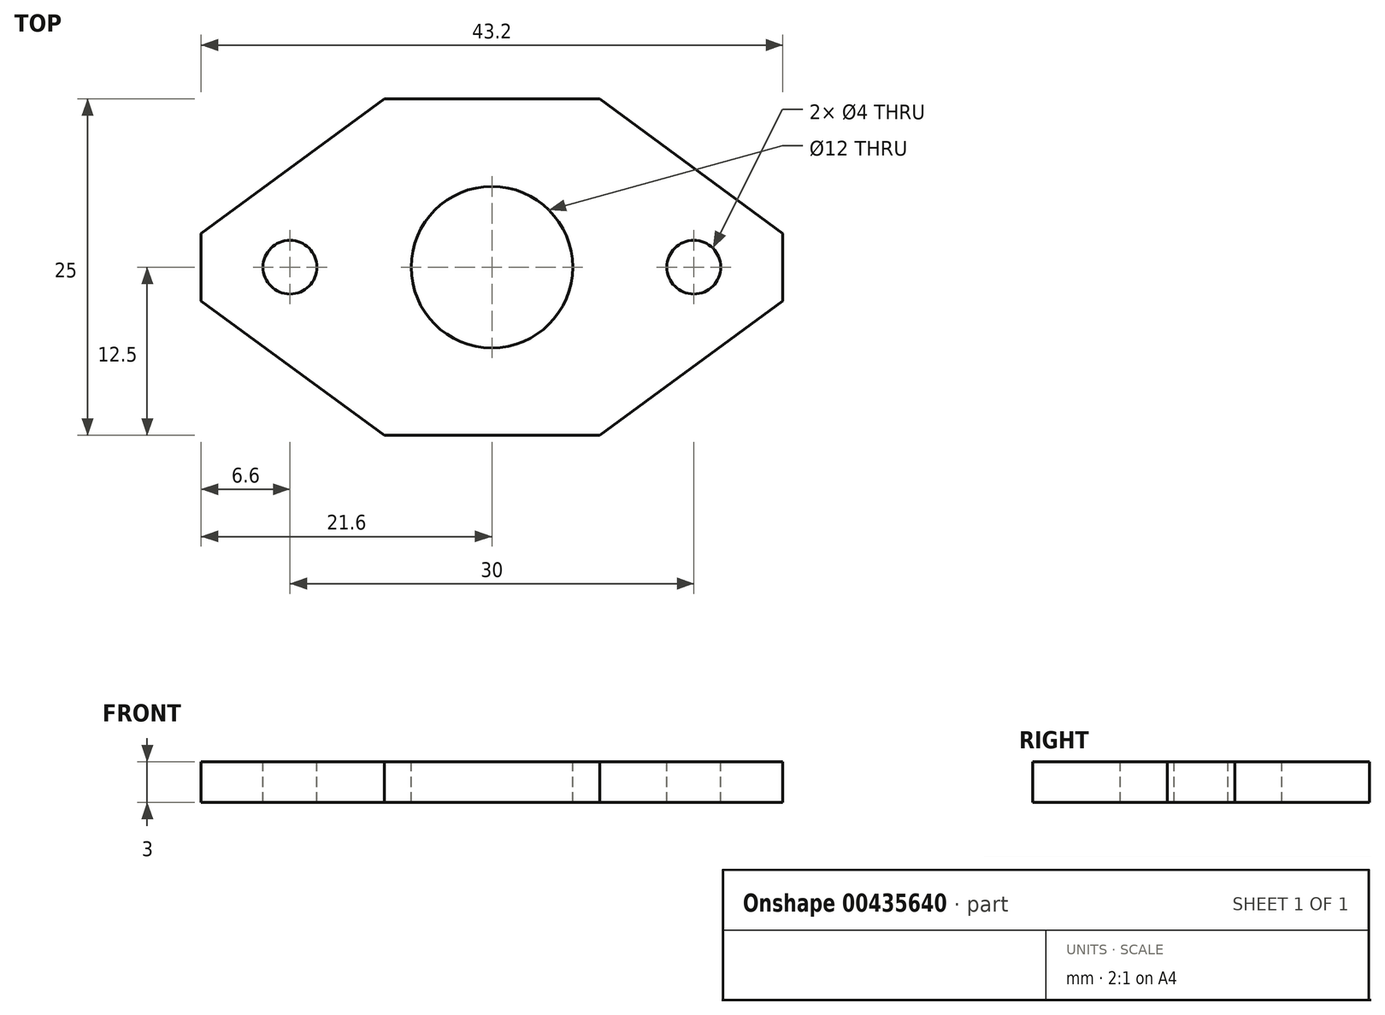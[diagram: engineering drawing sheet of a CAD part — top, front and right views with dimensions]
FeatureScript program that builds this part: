
annotation { "Feature Type Name" : "Feature", "Feature Type Description" : "" }
export const myFeature = defineFeature(function(context is Context, id is Id, definition is map)
    precondition{}
    {
        {
            var Q0;
            Q0=qCreatedBy(makeId("Top.planeOp"),FACE);
            var sketch = newSketch(context, id + "F0", { "sketchPlane" : qUnion([Q0])});
            skLineSegment(sketch, "E0.bottom", {"start": v(25, 12.5) * mm, "end": v(-25, 12.5) * mm});
            skLineSegment(sketch, "E0.top", {"start": v(25, -12.5) * mm, "end": v(-25, -12.5) * mm});
            skLineSegment(sketch, "E0.left", {"start": v(25, 12.5) * mm, "end": v(25, -12.5) * mm});
            skLineSegment(sketch, "E0.right", {"start": v(-25, 12.5) * mm, "end": v(-25, -12.5) * mm});
            skPoint(sketch, "E0.middle", {"position": v(0, 0) * mm});
            skSolve(sketch);
        }
        {
            var Q0;
            Q0=makeQuery(id+"F0.imprint","IMPRINT",FACE,{"disambiguationData":[TD([[makeQuery(id+"F0.imprint","IMPRINT",EDGE,{"derivedFrom":sQuery(id+"F0.wireOp",EDGE,"E0.bottom")}),1.0]])]});
            extrude(context, id + "F1", {"entities" : qUnion([Q0]), "depth" : 3 * mm});
        }
        {
            var Q0;
            Q0=makeQuery(id+"F1.opExtrude","CAP_FACE",FACE,{"disambiguationData":[OSD([sQuery(id+"F0.wireOp",EDGE,"E0.bottom"),sQuery(id+"F0.wireOp",EDGE,"E0.top"),sQuery(id+"F0.wireOp",EDGE,"E0.left"),sQuery(id+"F0.wireOp",EDGE,"E0.right")])],"isStart":false});
            var sketch = newSketch(context, id + "F2", { "sketchPlane" : qUnion([Q0])});
            skCircle(sketch, "E1", {"center": v(0, 0) * mm, "radius": 6 * mm});
            skSolve(sketch);
        }
        {
            var Q0;
            Q0=makeQuery(id+"F2.imprint","IMPRINT",FACE,{"disambiguationData":[TD([[makeQuery(id+"F2.imprint","IMPRINT",EDGE,{"derivedFrom":sQuery(id+"F2.wireOp",EDGE,"E1")}),1.0]])]});
            extrude(context, id + "F3", {"entities" : qUnion([Q0]), "operationType" : NewBodyOperationType.REMOVE, "endBound" : BoundingType.THROUGH_ALL, "oppositeDirection" : true, "depth" : 25 * mm});
        }
        {
            var Q0;
            Q0=makeQuery(id+"F1.opExtrude","CAP_FACE",FACE,{"disambiguationData":[OSD([sQuery(id+"F0.wireOp",EDGE,"E0.bottom"),sQuery(id+"F0.wireOp",EDGE,"E0.top"),sQuery(id+"F0.wireOp",EDGE,"E0.left"),sQuery(id+"F0.wireOp",EDGE,"E0.right")])],"isStart":false});
            var sketch = newSketch(context, id + "F4", { "sketchPlane" : qUnion([Q0])});
            skLineSegment(sketch, "E2", {"start": v(-25, 0) * mm, "end": v(-8, 12.5) * mm});
            skLineSegment(sketch, "E3", {"start": v(-25, 0) * mm, "end": v(-8, -12.5) * mm});
            skLineSegment(sketch, "E4", {"start": v(8, 12.5) * mm, "end": v(25, 0) * mm});
            skLineSegment(sketch, "E5", {"start": v(25, 0) * mm, "end": v(8, -12.5) * mm});
            skLineSegment(sketch, "E6", {"start": v(-8, 12.5) * mm, "end": v(8, 12.5) * mm});
            skLineSegment(sketch, "E7", {"start": v(8, -12.5) * mm, "end": v(-8, -12.5) * mm});
            skSolve(sketch);
        }
        {
            var Q0;
            {var subQ0=sQuery(id+"F4.wireOp",EDGE,"E2");Q0=makeQuery(id+"F4.imprint","IMPRINT",FACE,{"disambiguationData":[TD([[makeQuery(id+"F4.imprint","IMPRINT",EDGE,{"derivedFrom":subQ0}),1.0]])]});}
            var Q1;
            {var subQ0=sQuery(id+"F4.wireOp",EDGE,"E3");Q1=makeQuery(id+"F4.imprint","IMPRINT",FACE,{"disambiguationData":[TD([[makeQuery(id+"F4.imprint","IMPRINT",EDGE,{"derivedFrom":subQ0}),-1.0]])]});}
            var Q2;
            {var subQ0=sQuery(id+"F4.wireOp",EDGE,"E4");Q2=makeQuery(id+"F4.imprint","IMPRINT",FACE,{"disambiguationData":[TD([[makeQuery(id+"F4.imprint","IMPRINT",EDGE,{"derivedFrom":subQ0}),1.0]])]});}
            var Q3;
            {var subQ0=sQuery(id+"F4.wireOp",EDGE,"E5");Q3=makeQuery(id+"F4.imprint","IMPRINT",FACE,{"disambiguationData":[TD([[makeQuery(id+"F4.imprint","IMPRINT",EDGE,{"derivedFrom":subQ0}),1.0]])]});}
            extrude(context, id + "F5", {"entities" : qUnion([Q0, Q1, Q2, Q3]), "operationType" : NewBodyOperationType.REMOVE, "endBound" : BoundingType.THROUGH_ALL, "oppositeDirection" : true, "depth" : 25 * mm});
        }
        {
            var Q0;
            Q0=makeQuery(id+"F1.opExtrude","CAP_FACE",FACE,{"disambiguationData":[OSD([sQuery(id+"F0.wireOp",EDGE,"E0.bottom"),sQuery(id+"F0.wireOp",EDGE,"E0.top"),sQuery(id+"F0.wireOp",EDGE,"E0.left"),sQuery(id+"F0.wireOp",EDGE,"E0.right")])],"isStart":false});
            var sketch = newSketch(context, id + "F6", { "sketchPlane" : qUnion([Q0])});
            skCircle(sketch, "E8", {"center": v(-15, 0) * mm, "radius": 2 * mm});
            skCircle(sketch, "E9", {"center": v(15, 0) * mm, "radius": 2 * mm});
            skSolve(sketch);
        }
        {
            var Q0;
            Q0 = qSketchRegion(id + "F6", true);
            extrude(context, id + "F7", {"entities" : qUnion([Q0]), "operationType" : NewBodyOperationType.REMOVE, "endBound" : BoundingType.THROUGH_ALL, "oppositeDirection" : true, "depth" : 25 * mm});
        }
        {
            var Q0;
            Q0=makeQuery(id+"F1.opExtrude","CAP_FACE",FACE,{"disambiguationData":[OSD([sQuery(id+"F0.wireOp",EDGE,"E0.bottom"),sQuery(id+"F0.wireOp",EDGE,"E0.top"),sQuery(id+"F0.wireOp",EDGE,"E0.left"),sQuery(id+"F0.wireOp",EDGE,"E0.right")])],"isStart":false});
            var sketch = newSketch(context, id + "F8", { "sketchPlane" : qUnion([Q0])});
            skLineSegment(sketch, "E10", {"start": v(-21.6, 2.5) * mm, "end": v(-21.6, -2.5) * mm});
            skLineSegment(sketch, "E11", {"start": v(21.6, 2.5) * mm, "end": v(21.6, -2.5) * mm});
            skSolve(sketch);
        }
        {
            var Q0;
            {var subQ0=sQuery(id+"F8.wireOp",EDGE,"E10");Q0=makeQuery(id+"F8.imprint","IMPRINT",FACE,{"disambiguationData":[TD([[makeQuery(id+"F8.imprint","IMPRINT",EDGE,{"derivedFrom":subQ0}),-1.0]])]});}
            var Q1;
            {var subQ0=sQuery(id+"F8.wireOp",EDGE,"E11");Q1=makeQuery(id+"F8.imprint","IMPRINT",FACE,{"disambiguationData":[TD([[makeQuery(id+"F8.imprint","IMPRINT",EDGE,{"derivedFrom":subQ0}),1.0]])]});}
            extrude(context, id + "F9", {"entities" : qUnion([Q0, Q1]), "operationType" : NewBodyOperationType.REMOVE, "endBound" : BoundingType.THROUGH_ALL, "oppositeDirection" : true, "depth" : 25 * mm});
        }
    });
